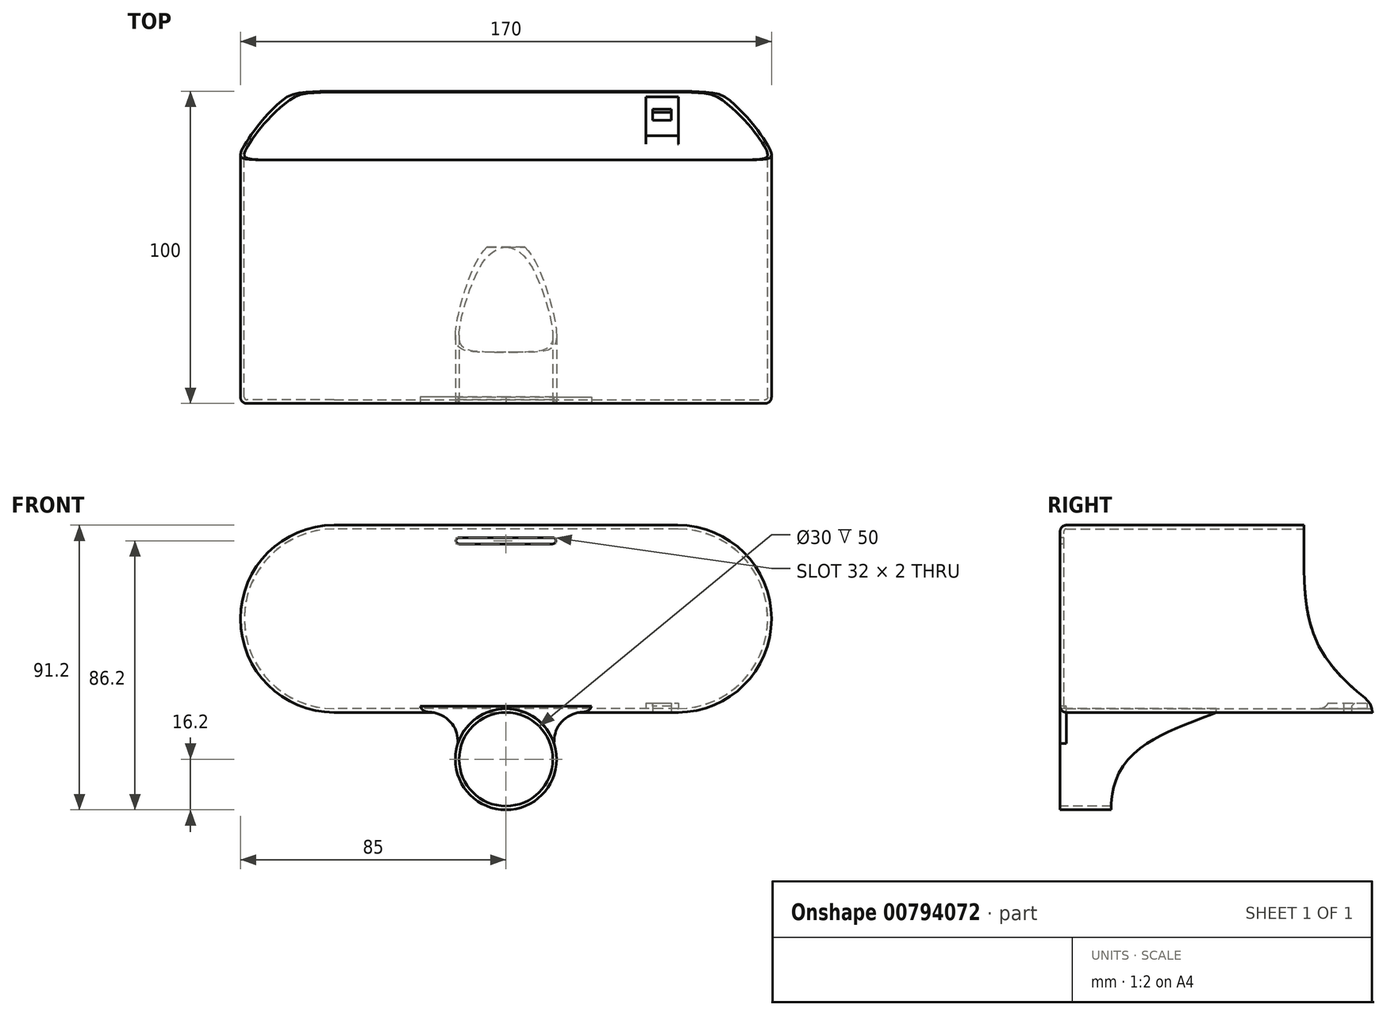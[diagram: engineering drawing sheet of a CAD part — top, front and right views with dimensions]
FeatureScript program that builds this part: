
annotation { "Feature Type Name" : "Feature", "Feature Type Description" : "" }
export const myFeature = defineFeature(function(context is Context, id is Id, definition is map)
    precondition{}
    {
        {
            var Q0;
            Q0=qCreatedBy(makeId("Front.planeOp"),FACE);
            var sketch = newSketch(context, id + "F0", { "sketchPlane" : qUnion([Q0])});
            skLineSegment(sketch, "E0.bottom", {"start": v(-55, 0) * mm, "end": v(55, 0) * mm});
            skLineSegment(sketch, "E0.top", {"start": v(-55, 60) * mm, "end": v(55, 60) * mm});
            skLineSegment(sketch, "E0.left", {"start": v(-55, 0) * mm, "end": v(-55, 60) * mm});
            skLineSegment(sketch, "E0.right", {"start": v(55, 0) * mm, "end": v(55, 60) * mm});
            skArc(sketch, "E1", {"start": v(-55, 60) * mm, "mid": v(-85, 30) * mm, "end": v(-55, 0) * mm});
            skArc(sketch, "E2", {"start": v(55, 0) * mm, "mid": v(85, 30) * mm, "end": v(55, 60) * mm});
            skSolve(sketch);
        }
        {
            var Q0;
            Q0 = qSketchRegion(id + "F0", true);
            extrude(context, id + "F1", {"entities" : qUnion([Q0]), "depth" : 100 * mm, "offsetDistance" : 25 * mm});
        }
        {
            var Q0;
            Q0=qCreatedBy(makeId("Right.planeOp"),FACE);
            var sketch = newSketch(context, id + "F2", { "sketchPlane" : qUnion([Q0])});
            skFitSpline(sketch, "E3", {"points": [v(0, 0) * mm, v(-3, 5.13) * mm, v(-17.9, 22.72) * mm, v(-22, 60) * mm], "startDerivative": vector(-10.6, 54.34) * mm, "endDerivative": vector(-1.22, 79.26) * mm});
            skLineSegment(sketch, "E4", {"start": v(-22, 60) * mm, "end": v(12.53, 60) * mm});
            skLineSegment(sketch, "E5", {"start": v(12.53, 60) * mm, "end": v(12.53, 0) * mm});
            skLineSegment(sketch, "E6", {"start": v(12.53, 0) * mm, "end": v(0, 0) * mm});
            skSolve(sketch);
        }
        {
            var Q0;
            Q0=makeQuery(id+"F2.imprint","IMPRINT",FACE,{"disambiguationData":[TD([[makeQuery(id+"F2.imprint","IMPRINT",EDGE,{"derivedFrom":sQuery(id+"F2.wireOp",EDGE,"E3")}),-1.0]])]});
            extrude(context, id + "F3", {"entities" : qUnion([Q0]), "operationType" : NewBodyOperationType.REMOVE, "endBound" : BoundingType.SYMMETRIC, "depth" : 200 * mm, "offsetDistance" : 25 * mm});
        }
        {
            var Q0;
            Q0=makeQuery(id+"F1.opExtrude","CAP_FACE",FACE,{"disambiguationData":[OSD([sQuery(id+"F0.wireOp",EDGE,"E0.bottom"),sQuery(id+"F0.wireOp",EDGE,"E0.top"),sQuery(id+"F0.wireOp",EDGE,"E0.left"),sQuery(id+"F0.wireOp",EDGE,"E0.right")])],"isStart":false});
            fillet(context, id + "F4", {"entities" : qUnion([Q0]), "radius" : 2 * mm, "tangentPropagation" : true, "allowEdgeOverflow" : false});
        }
        {
            var Q0;
            Q0=makeQuery(id+"F3.boolean.opBoolean","COPY",FACE,{"derivedFrom":makeQuery(id+"F3.opExtrude","SWEPT_FACE",FACE,{"disambiguationData":[OSD([sQuery(id+"F2.wireOp",EDGE,"E3")])]})});
            shell(context, id + "F5", {"entities" : qUnion([Q0]), "thickness" : 1.2 * mm});
        }
        {
            var Q0;
            Q0=qCreatedBy(makeId("Top.planeOp"),FACE);
            var sketch = newSketch(context, id + "F6", { "sketchPlane" : qUnion([Q0])});
            skLineSegment(sketch, "E7.bottom", {"start": v(47, -9.25) * mm, "end": v(53, -9.25) * mm});
            skLineSegment(sketch, "E7.top", {"start": v(47, -6.75) * mm, "end": v(53, -6.75) * mm});
            skLineSegment(sketch, "E7.left", {"start": v(47, -9.25) * mm, "end": v(47, -6.75) * mm});
            skLineSegment(sketch, "E7.right", {"start": v(53, -9.25) * mm, "end": v(53, -6.75) * mm});
            skPoint(sketch, "E7.middle", {"position": v(50, -8) * mm});
            skLineSegment(sketch, "E8.bottom", {"start": v(44.8, -14.22) * mm, "end": v(55.2, -14.22) * mm});
            skLineSegment(sketch, "E8.top", {"start": v(44.8, -1.78) * mm, "end": v(55.2, -1.78) * mm});
            skLineSegment(sketch, "E8.left", {"start": v(44.8, -14.22) * mm, "end": v(44.8, -1.78) * mm});
            skLineSegment(sketch, "E8.right", {"start": v(55.2, -14.22) * mm, "end": v(55.2, -1.78) * mm});
            skSolve(sketch);
        }
        {
            var Q0;
            Q0=makeQuery(id+"F6.imprint","IMPRINT",FACE,{"disambiguationData":[TD([[makeQuery(id+"F6.imprint","IMPRINT",EDGE,{"derivedFrom":sQuery(id+"F6.wireOp",EDGE,"E7.bottom")}),-1.0]])]});
            extrude(context, id + "F7", {"entities" : qUnion([Q0]), "operationType" : NewBodyOperationType.ADD, "depth" : 3 * mm, "offsetDistance" : 25 * mm});
        }
        {
            var Q0;
            Q0=makeQuery(id+"F6.imprint","IMPRINT",FACE,{"disambiguationData":[TD([[makeQuery(id+"F6.imprint","IMPRINT",EDGE,{"derivedFrom":sQuery(id+"F6.wireOp",EDGE,"E7.bottom")}),1.0]])]});
            extrude(context, id + "F8", {"entities" : qUnion([Q0]), "operationType" : NewBodyOperationType.REMOVE, "endBound" : BoundingType.SYMMETRIC, "oppositeDirection" : true, "depth" : 20 * mm, "offsetDistance" : 25 * mm});
        }
        {
            var Q0;
            {var subQ0=sQuery(id+"F0.wireOp",EDGE,"E0.bottom");Q0=makeQuery(id+"F7.boolean.opBoolean","INTERSECT",EDGE,{"derivedFrom":[makeQuery(id+"F5.opShell","OFFSET_FACE",FACE,{"disambiguationData":[OSD([subQ0]),TDD([makeQuery(id+"F1.opExtrude","SWEPT_FACE",FACE,{"disambiguationData":[OSD([subQ0])]})])]}),makeQuery(id+"F7.opExtrude","SWEPT_FACE",FACE,{"disambiguationData":[OSD([sQuery(id+"F6.wireOp",EDGE,"E8.bottom")])]})]});}
            fillet(context, id + "F9", {"entities" : qUnion([Q0]), "radius" : 3 * mm, "tangentPropagation" : true, "allowEdgeOverflow" : false});
        }
        {
            var Q0;
            Q0=makeQuery(id+"F7.opExtrude","CAP_EDGE",EDGE,{"disambiguationData":[OSD([sQuery(id+"F6.wireOp",EDGE,"E7.top")])],"isStart":false});
            chamfer(context, id + "F10", {"entities" : qUnion([Q0]), "width" : 1 * mm, "tangentPropagation" : true});
        }
        {
            var Q0;
            Q0=makeQuery(id+"F1.opExtrude","CAP_FACE",FACE,{"disambiguationData":[OSD([sQuery(id+"F0.wireOp",EDGE,"E0.bottom"),sQuery(id+"F0.wireOp",EDGE,"E0.top"),sQuery(id+"F0.wireOp",EDGE,"E1"),sQuery(id+"F0.wireOp",EDGE,"E2")])],"isStart":false});
            var sketch = newSketch(context, id + "F11", { "sketchPlane" : qUnion([Q0])});
            skCircle(sketch, "E9", {"center": v(0, -15) * mm, "radius": 15 * mm});
            skCircle(sketch, "E10", {"center": v(0, -15) * mm, "radius": 16.2 * mm});
            skFitSpline(sketch, "E11", {"points": [v(15.37, -9.9) * mm, v(17.14, -3.82) * mm, v(23.2, 0) * mm, v(27.43, 2) * mm], "startDerivative": vector(0.73, 20.08) * mm, "endDerivative": vector(11.1, 23.12) * mm});
            skLineSegment(sketch, "E12", {"start": v(0, 0) * mm, "end": v(0, 2) * mm});
            skSolve(sketch);
        }
        {
            var Q0;
            {var subQ0=sQuery(id+"F11.wireOp",EDGE,"j0CPto9W-Aohg-HQX4-fcGy-ZsRNIFiT2zVB");var subQ1=sQuery(id+"F11.wireOp",EDGE,"E9");var subQ2=makeQuery(id+"F11.imprint","INTERSECT",VERTEX,{"derivedFrom":[subQ1,subQ0]});Q0=makeQuery(id+"F11.imprint","IMPRINT",FACE,{"disambiguationData":[TD([[makeQuery(id+"F11.imprint","IMPRINT",EDGE,{"disambiguationData":[TD([[subQ2,-1.0]])],"derivedFrom":subQ1}),-1.0]])]});}
            var Q1;
            {var subQ0=sQuery(id+"F11.wireOp",EDGE,"j0CPto9W-Aohg-HQX4-fcGy-ZsRNIFiT2zVB");var subQ1=sQuery(id+"F11.wireOp",EDGE,"E9");var subQ2=makeQuery(id+"F11.imprint","INTERSECT",VERTEX,{"derivedFrom":[subQ1,subQ0]});Q1=makeQuery(id+"F11.imprint","IMPRINT",FACE,{"disambiguationData":[TD([[makeQuery(id+"F11.imprint","IMPRINT",EDGE,{"disambiguationData":[TD([[subQ2,1.0]])],"derivedFrom":subQ1}),-1.0]])]});}
            extrude(context, id + "F12", {"entities" : qUnion([Q0, Q1]), "oppositeDirection" : true, "depth" : 50 * mm, "offsetDistance" : 25 * mm});
        }
        {
            var Q0;
            Q0=qCreatedBy(makeId("Right.planeOp"),FACE);
            var sketch = newSketch(context, id + "F13", { "sketchPlane" : qUnion([Q0])});
            skLineSegment(sketch, "E13", {"start": v(-70.16, 0) * mm, "end": v(-50, 0) * mm});
            skLineSegment(sketch, "E14", {"start": v(-50, 0) * mm, "end": v(-50, -50.17) * mm});
            skFitSpline(sketch, "E15", {"points": [v(-50, 0) * mm, v(-66.8, -6.9) * mm, v(-82.24, -21.88) * mm, v(-79.6, -44.45) * mm, v(-73.89, -49.68) * mm], "startDerivative": vector(-50.32, -21.92) * mm, "endDerivative": vector(1.11, -43.4) * mm});
            skLineSegment(sketch, "E16", {"start": v(-50, -50.17) * mm, "end": v(-73.89, -49.68) * mm});
            skSolve(sketch);
        }
        {
            var Q0;
            Q0 = qSketchRegion(id + "F13", true);
            extrude(context, id + "F14", {"entities" : qUnion([Q0]), "operationType" : NewBodyOperationType.REMOVE, "endBound" : BoundingType.SYMMETRIC, "oppositeDirection" : true, "depth" : 50 * mm, "offsetDistance" : 25 * mm});
        }
        {
            var Q0;
            Q0=qCreatedBy(makeId("Right.planeOp"),FACE);
            var sketch = newSketch(context, id + "F15", { "sketchPlane" : qUnion([Q0])});
            skLineSegment(sketch, "E17", {"start": v(-80, 0) * mm, "end": v(-100, 20) * mm});
            skSolve(sketch);
        }
        {
            var Q0;
            {var subQ0=sQuery(id+"F11.wireOp",EDGE,"E11");Q0=makeQuery(id+"F11.imprint","IMPRINT",FACE,{"disambiguationData":[TD([[makeQuery(id+"F11.imprint","IMPRINT",EDGE,{"derivedFrom":subQ0}),1.0]])]});}
            extrude(context, id + "F16", {"entities" : qUnion([Q0]), "oppositeDirection" : true, "depth" : 2 * mm, "offsetDistance" : 25 * mm});
        }
        {
            var Q0;
            Q0=makeQuery(id+"F16.opExtrude","SWEPT_BODY",BODY,{"disambiguationData":[OSD([sQuery(id+"F0.wireOp",EDGE,"E0.bottom"),sQuery(id+"F0.wireOp",EDGE,"E0.top"),sQuery(id+"F0.wireOp",EDGE,"E1"),sQuery(id+"F0.wireOp",EDGE,"E2"),sQuery(id+"F11.wireOp",EDGE,"E10"),sQuery(id+"F11.wireOp",EDGE,"E11"),sQuery(id+"F11.wireOp",EDGE,"E12")])]});
            var Q1;
            Q1=qCreatedBy(makeId("Right.planeOp"),FACE);
            mirror(context, id + "F17", {"entities" : qUnion([Q0]), "mirrorPlane" : qUnion([Q1])});
        }
        {
            var Q0;
            {var subQ0=sQuery(id+"F0.wireOp",EDGE,"E2");var subQ1=sQuery(id+"F0.wireOp",EDGE,"E1");var subQ2=sQuery(id+"F0.wireOp",EDGE,"E0.top");var subQ3=sQuery(id+"F0.wireOp",EDGE,"E0.bottom");var subQ4=makeQuery(id+"F1.opExtrude","CAP_FACE",FACE,{"disambiguationData":[OSD([subQ3,subQ2,subQ1,subQ0])],"isStart":false});Q0=makeQuery(id+"F11.imprint","IMPRINT",FACE,{"disambiguationData":[TD([[makeQuery(id+"F11.imprint","IMPRINT",EDGE,{"derivedFrom":makeQuery(id+"F4.opFillet","BLEND_EDGE",EDGE,{"blendedFrom":[makeQuery(id+"F1.opExtrude","CAP_EDGE",EDGE,{"disambiguationData":[OSD([subQ2])],"isStart":false}),subQ4],"blendedInto":[subQ4]})}),1.0]])]});}
            var sketch = newSketch(context, id + "F18", { "sketchPlane" : qUnion([Q0])});
            skLineSegment(sketch, "E18", {"start": v(15, 55) * mm, "end": v(-15, 55) * mm});
            skArc(sketch, "E19.0.startCap", {"start": v(15, 56) * mm, "mid": v(16, 55) * mm, "end": v(15, 54) * mm});
            skArc(sketch, "E19.0.endCap", {"start": v(-15, 54) * mm, "mid": v(-16, 55) * mm, "end": v(-15, 56) * mm});
            skLineSegment(sketch, "E19.0.left", {"start": v(15, 54) * mm, "end": v(-15, 54) * mm});
            skLineSegment(sketch, "E19.0.right", {"start": v(15, 56) * mm, "end": v(-15, 56) * mm});
            skSolve(sketch);
        }
        {
            var Q0;
            Q0 = qSketchRegion(id + "F18", true);
            extrude(context, id + "F19", {"entities" : qUnion([Q0]), "operationType" : NewBodyOperationType.REMOVE, "oppositeDirection" : true, "depth" : 25 * mm, "offsetDistance" : 25 * mm});
        }
    });
